# Revit family: HB-8000C-B1
name_source: partatom
category: 衛工裝置
revit_build: Autodesk Revit 2015 (Build: 20140223_1515(x64)
units: mm (PartAtom-declared; Revit-internal decimal feet)

## types (2) — shared parameters
ADA Compliance = Yes - Flush Valve
Back Up Power = None
Brushed Nickel (PVD) Valve Finish = 否
CL of Supply Above Top of Fixture = 11 1/2"
CL of Supply to Centerline of Valve = 4 3/4"
CW 接頭 = 是
Flush Choice = Single Flush
HW 接頭 = 否
Inlet Spud Size = 3/4" I.P.S.
Inlet Supply Size = 3/4"
Manual Override = 是
Mounting = Exposed
OA Height Above Top of Fixture = 16"
Operation = Automatic
Polished Brass (PVD) Valve Finish = 是
Polished Chrome Valve Finish = 是
Power Source = AA Alkaline Battery x 4 pcs
Sensor Type = Active Infrared
Spud Location = Exposed Top
URL = www.hydrotekintl.com
Valve Body = Chrome Plated
Valve Body, Tailpiece and Control Stop = Semi-Red Brass, ASSE 1037, ANSI/ASME A112.19.2
Valve Cover = Engineered Metal
Valve Type = Piston
Warranty = 3 Years (Limited)
廢水口接頭 = 否
製造商 = Hydrotek International, Inc.
通風口接頭 = 否
關鍵註記 = Sensor Operated Flush Valve for Urinal

## per-type parameters (varying)
| type | Flush Cycle Water Usage | 描述 |
| HB-8000C-B1 | 1.0 Gpf /3.75 Lpf | Exposed, Battery Type, Sensor Operated HB-8000C-B1 Water Urinal Flush Valve |
| HB8-B1-0125 | 0.125 Gpf /0.47 Lpf | Exposed, Battery Type, Sensor Operated HB8-B1-0125 Water Urinal Flush Valve |

note: column(s) folded — value = type name in every type: 模型

## geometry (parser evidence)
native form markers: Sweep x5
no freeform markers — native parametric forms only
